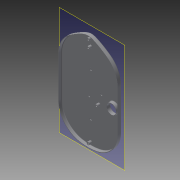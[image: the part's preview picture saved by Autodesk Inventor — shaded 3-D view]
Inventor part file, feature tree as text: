
AUTODESK INVENTOR PART (.ipt)
format: ipt  version: 2014 (Build 180170000, 170)  size: 619,520 bytes
history: native  units: mm
features: extrude x10, sketch x10, other x4, fillet x4, projected_geometry x2
ambient origin geometry x8: Origin, YZ Plane, XZ Plane, XY Plane, X Axis, Y Axis, Z Axis, Center Point
bodies: Body1 (feature_tree)
feature tree (30):
  other  "body.ipt"
  extrude  "押し出し2"  Depth=10.0mm
  other  "作業平面1"
  extrude  "押し出し3"  Depth=30.0mm TaperAngle=0.0deg
  extrude  "押し出し4"  Depth=2.0mm
  extrude  "押し出し5"  Depth=30.0mm TaperAngle=0.0deg
  extrude  "押し出し6"  Depth=2.0mm TaperAngle=0.0deg
  extrude  "押し出し7"  Depth=5.2mm
  fillet  "フィレット3"  Radius=5.2mm
  fillet  "フィレット4"  Radius=5.2mm
  extrude  "押し出し15"  Depth=5.2mm
  extrude  "押し出し14"  Depth=3.0mm TaperAngle=0.0deg
  extrude  "押し出し16"  Depth=1.0mm TaperAngle=0.0deg
  extrude  "押し出し17"  Depth=1.0mm
  fillet  "フィレット6"  Radius=5.6mm
  fillet  "フィレット7"  Radius=1.0mm
  other  "ソリッド1::body.ipt"
  other  "TaggingFeature8"
  sketch  "スケッチ5"
  sketch  "スケッチ7"
  sketch  "スケッチ8"
  sketch  "スケッチ10"
  sketch  "スケッチ11"
  sketch  "スケッチ12"
  sketch  "スケッチ22"
  projected_geometry  "投影ループ10"
  sketch  "スケッチ23"
  sketch  "スケッチ24"
  projected_geometry  "投影ループ11"
  sketch  "スケッチ25"
